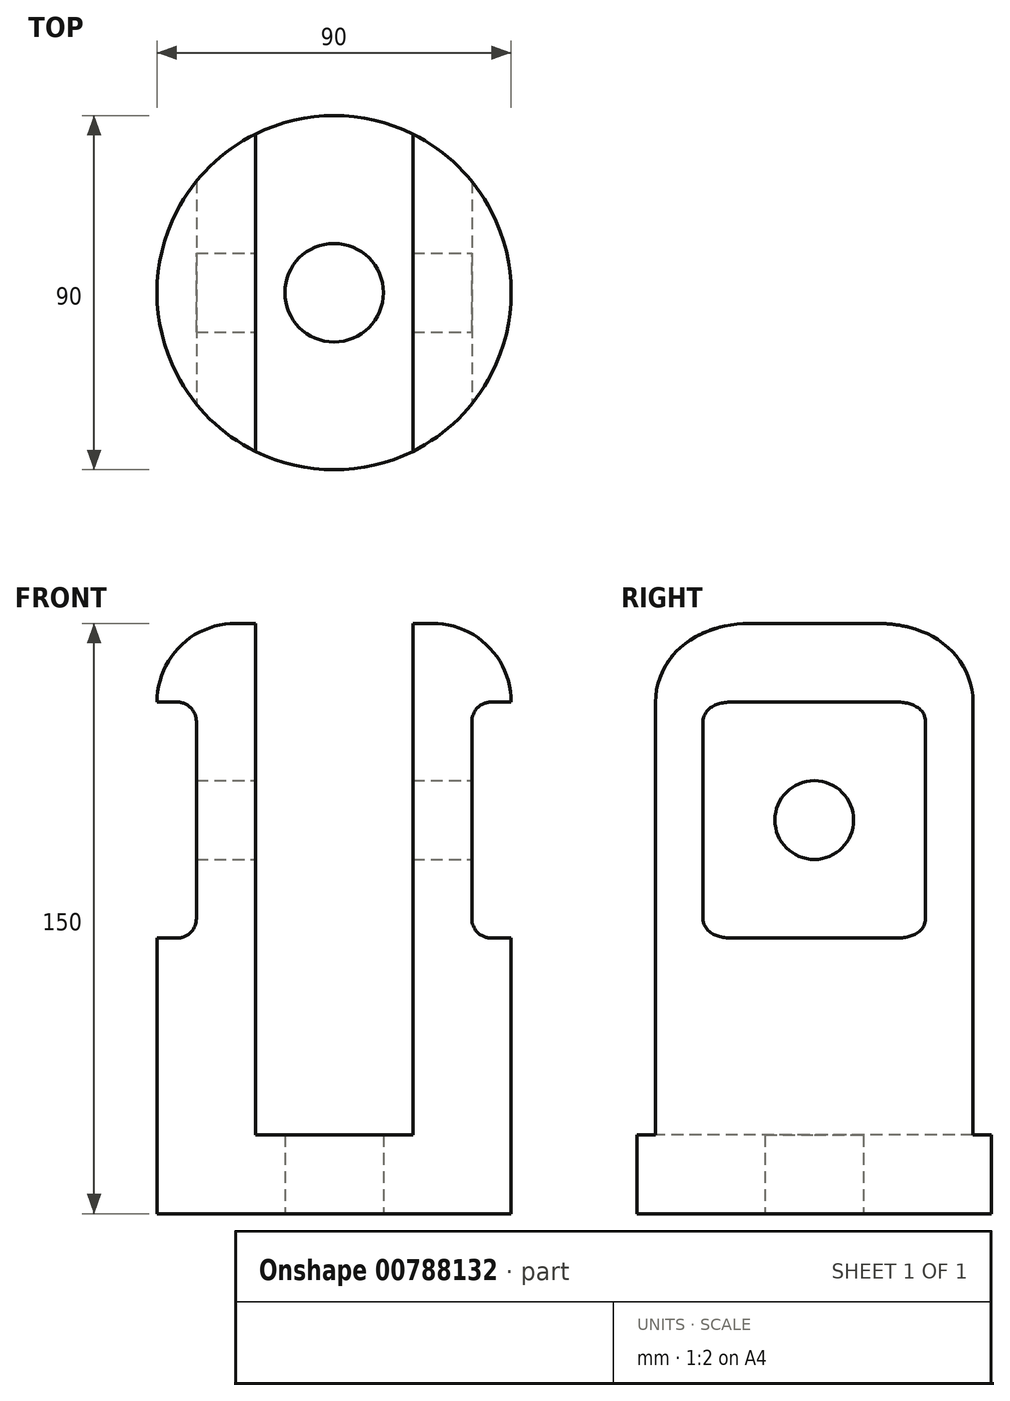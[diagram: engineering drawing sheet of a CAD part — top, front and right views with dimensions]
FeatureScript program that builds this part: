
annotation { "Feature Type Name" : "Feature", "Feature Type Description" : "" }
export const myFeature = defineFeature(function(context is Context, id is Id, definition is map)
    precondition{}
    {
        {
            var Q0;
            Q0=qCreatedBy(makeId("Top.planeOp"),FACE);
            var sketch = newSketch(context, id + "F0", { "sketchPlane" : qUnion([Q0])});
            skCircle(sketch, "E0", {"center": v(0, 0) * mm, "radius": 45 * mm});
            skCircle(sketch, "E1", {"center": v(0, 0) * mm, "radius": 12.5 * mm});
            skSolve(sketch);
        }
        {
            var Q0;
            Q0 = qSketchRegion(id + "F0", true);
            extrude(context, id + "F1", {"entities" : qUnion([Q0]), "depth" : 150 * mm, "offsetDistance" : 25 * mm});
        }
        {
            var Q0;
            Q0=qCreatedBy(makeId("Front.planeOp"),FACE);
            var sketch = newSketch(context, id + "F2", { "sketchPlane" : qUnion([Q0])});
            skLineSegment(sketch, "E2.bottom", {"start": v(-20, 170) * mm, "end": v(20, 170) * mm});
            skLineSegment(sketch, "E2.top", {"start": v(-20, 20) * mm, "end": v(20, 20) * mm});
            skLineSegment(sketch, "E2.left", {"start": v(-20, 170) * mm, "end": v(-20, 20) * mm});
            skLineSegment(sketch, "E2.right", {"start": v(20, 170) * mm, "end": v(20, 20) * mm});
            skPoint(sketch, "E3", {"position": v(0, 20) * mm});
            skLineSegment(sketch, "E4.bottom", {"start": v(-57.36, 130) * mm, "end": v(-35, 130) * mm});
            skLineSegment(sketch, "E4.top", {"start": v(-57.36, 70) * mm, "end": v(-35, 70) * mm});
            skLineSegment(sketch, "E4.left", {"start": v(-57.36, 130) * mm, "end": v(-57.36, 70) * mm});
            skLineSegment(sketch, "E4.right", {"start": v(-35, 130) * mm, "end": v(-35, 70) * mm});
            skLineSegment(sketch, "E5.MirrorCS", {"start": v(35, 130) * mm, "end": v(35, 70) * mm});
            skLineSegment(sketch, "E6.MirrorCS", {"start": v(57.36, 130) * mm, "end": v(35, 130) * mm});
            skLineSegment(sketch, "E7.MirrorCS", {"start": v(57.36, 130) * mm, "end": v(57.36, 70) * mm});
            skLineSegment(sketch, "E8.MirrorCS", {"start": v(57.36, 70) * mm, "end": v(35, 70) * mm});
            skSolve(sketch);
        }
        {
            var Q0;
            Q0 = qSketchRegion(id + "F2", true);
            extrude(context, id + "F3", {"entities" : qUnion([Q0]), "operationType" : NewBodyOperationType.REMOVE, "oppositeDirection" : true, "depth" : 100 * mm, "offsetDistance" : 25 * mm, "hasSecondDirection" : true, "secondDirectionOppositeDirection" : false, "secondDirectionDepth" : 100 * mm});
        }
        {
            var Q0;
            {var subQ0=sQuery(id+"F0.wireOp",EDGE,"E0");Q0=makeQuery(id+"F3.boolean.opBoolean","SPLIT",EDGE,{"disambiguationData":[TD([makeQuery(id+"F3.opExtrude","SWEPT_FACE",FACE,{"disambiguationData":[OSD([sQuery(id+"F2.wireOp",EDGE,"E2.left")])]})])],"derivedFrom":makeQuery(id+"F1.opExtrude","CAP_EDGE",EDGE,{"disambiguationData":[OSD([subQ0])],"isStart":false})});}
            var Q1;
            {var subQ0=sQuery(id+"F0.wireOp",EDGE,"E0");Q1=makeQuery(id+"F3.boolean.opBoolean","SPLIT",EDGE,{"disambiguationData":[TD([makeQuery(id+"F3.opExtrude","SWEPT_FACE",FACE,{"disambiguationData":[OSD([sQuery(id+"F2.wireOp",EDGE,"E2.right")])]})])],"derivedFrom":makeQuery(id+"F1.opExtrude","CAP_EDGE",EDGE,{"disambiguationData":[OSD([subQ0])],"isStart":false})});}
            fillet(context, id + "F4", {"entities" : qUnion([Q0, Q1]), "radius" : 20 * mm, "tangentPropagation" : true, "allowEdgeOverflow" : false});
        }
        {
            var Q0;
            Q0=makeQuery(id+"F3.boolean.opBoolean","COPY",EDGE,{"derivedFrom":makeQuery(id+"F3.opExtrude","SWEPT_EDGE",EDGE,{"disambiguationData":[OSD([sQuery(id+"F2.wireOp",EDGE,"E4.bottom"),sQuery(id+"F2.wireOp",EDGE,"E4.right")])]})});
            var Q1;
            Q1=makeQuery(id+"F3.boolean.opBoolean","COPY",EDGE,{"derivedFrom":makeQuery(id+"F3.opExtrude","SWEPT_EDGE",EDGE,{"disambiguationData":[OSD([sQuery(id+"F2.wireOp",EDGE,"E4.top"),sQuery(id+"F2.wireOp",EDGE,"E4.right")])]})});
            var Q2;
            Q2=makeQuery(id+"F3.boolean.opBoolean","COPY",EDGE,{"derivedFrom":makeQuery(id+"F3.opExtrude","SWEPT_EDGE",EDGE,{"disambiguationData":[OSD([sQuery(id+"F2.wireOp",EDGE,"E5.MirrorCS"),sQuery(id+"F2.wireOp",EDGE,"E8.MirrorCS")])]})});
            var Q3;
            Q3=makeQuery(id+"F3.boolean.opBoolean","COPY",EDGE,{"derivedFrom":makeQuery(id+"F3.opExtrude","SWEPT_EDGE",EDGE,{"disambiguationData":[OSD([sQuery(id+"F2.wireOp",EDGE,"E5.MirrorCS"),sQuery(id+"F2.wireOp",EDGE,"E6.MirrorCS")])]})});
            fillet(context, id + "F5", {"entities" : qUnion([Q0, Q1, Q2, Q3]), "radius" : 5 * mm, "tangentPropagation" : true, "allowEdgeOverflow" : false});
        }
        {
            var Q0;
            Q0=makeQuery(id+"F3.boolean.opBoolean","COPY",FACE,{"derivedFrom":makeQuery(id+"F3.opExtrude","SWEPT_FACE",FACE,{"disambiguationData":[OSD([sQuery(id+"F2.wireOp",EDGE,"E5.MirrorCS")])]})});
            var sketch = newSketch(context, id + "F6", { "sketchPlane" : qUnion([Q0])});
            skCircle(sketch, "E9", {"center": v(0, 100) * mm, "radius": 10 * mm});
            skLineSegment(sketch, "E10", {"start": v(0, 125) * mm, "end": v(0, 75) * mm, "construction": true});
            skSolve(sketch);
        }
        {
            var Q0;
            Q0 = qSketchRegion(id + "F6", true);
            extrude(context, id + "F7", {"entities" : qUnion([Q0]), "operationType" : NewBodyOperationType.REMOVE, "oppositeDirection" : true, "depth" : 150 * mm, "offsetDistance" : 25 * mm});
        }
    });
